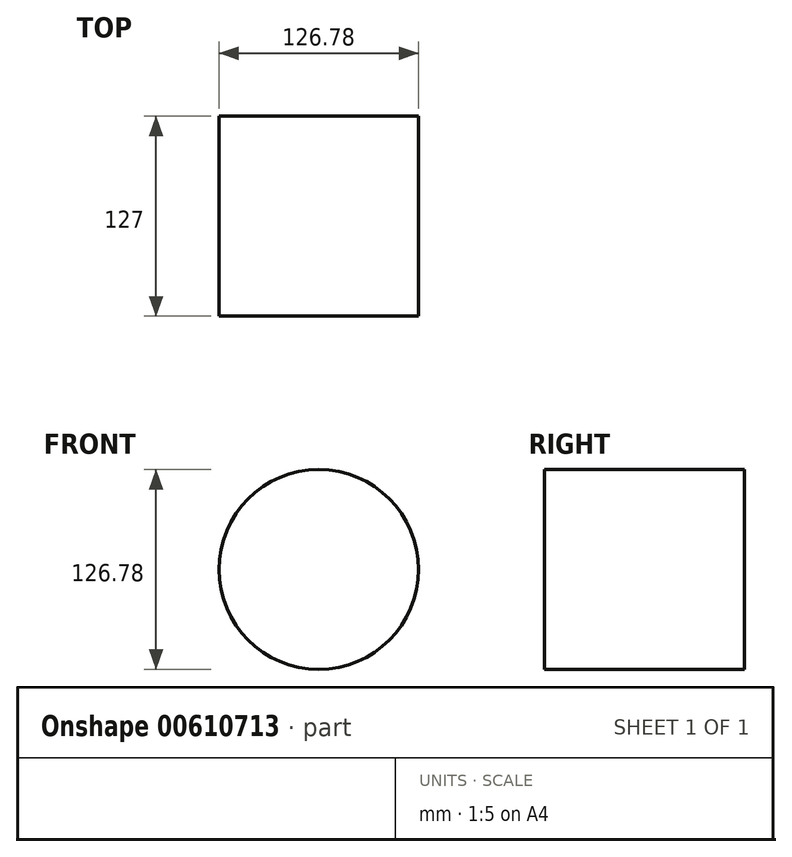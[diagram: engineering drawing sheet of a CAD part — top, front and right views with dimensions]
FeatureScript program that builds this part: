
annotation { "Feature Type Name" : "Feature", "Feature Type Description" : "" }
export const myFeature = defineFeature(function(context is Context, id is Id, definition is map)
    precondition{}
    {
        {
            var Q0;
            Q0=qCreatedBy(makeId("Front.planeOp"),FACE);
            var sketch = newSketch(context, id + "F0", { "sketchPlane" : qUnion([Q0])});
            skCircle(sketch, "E0", {"center": v(0, 0) * mm, "radius": 73.47 * mm});
            skCircle(sketch, "E1", {"center": v(0, 0) * mm, "radius": 61.5 * mm});
            skSolve(sketch);
        }
        {
            var Q0;
            Q0=sQuery(id+"F0.wireOp",EDGE,"E0");
            extrude(context, id + "F1", {"bodyType" : ToolBodyType.SURFACE, "surfaceEntities" : qUnion([Q0]), "depth" : 25.4 * mm, "offsetDistance" : 25.4 * mm});
        }
        {
            var Q0;
            Q0 = qSketchRegion(id + "F0", true);
            var sketch = newSketch(context, id + "F2", { "sketchPlane" : qUnion([Q0])});
            skCircle(sketch, "E2", {"center": v(0, 0) * mm, "radius": 63.39 * mm});
            skSolve(sketch);
        }
        {
            var Q0;
            Q0 = qSketchRegion(id + "F2", true);
            extrude(context, id + "F3", {"entities" : qUnion([Q0]), "depth" : 127 * mm, "offsetDistance" : 25.4 * mm});
        }
    });
